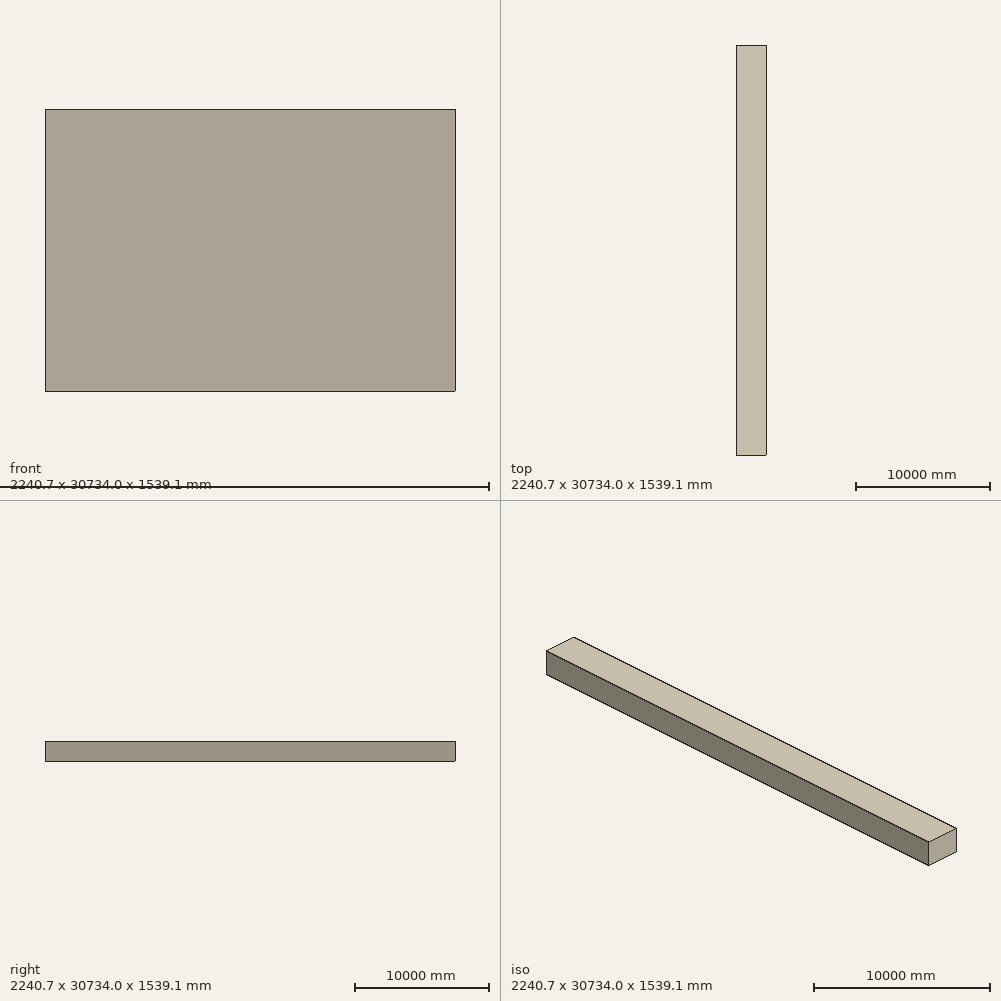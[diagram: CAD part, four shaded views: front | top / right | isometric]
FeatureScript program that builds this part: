
annotation { "Feature Type Name" : "Feature", "Feature Type Description" : "" }
export const myFeature = defineFeature(function(context is Context, id is Id, definition is map)
    precondition{}
    {
        {
            var Q0;
            Q0=qCreatedBy(makeId("Front.planeOp"),FACE);
            var sketch = newSketch(context, id + "F0", { "sketchPlane" : qUnion([Q0])});
            skLineSegment(sketch, "E0.bottom", {"start": v(-1032.38, 680.8) * mm, "end": v(1208.34, 680.8) * mm});
            skLineSegment(sketch, "E0.top", {"start": v(-1032.38, -858.27) * mm, "end": v(1208.34, -858.27) * mm});
            skLineSegment(sketch, "E0.left", {"start": v(-1032.38, 680.8) * mm, "end": v(-1032.38, -858.27) * mm});
            skLineSegment(sketch, "E0.right", {"start": v(1208.34, 680.8) * mm, "end": v(1208.34, -858.27) * mm});
            skSolve(sketch);
        }
        {
            var Q0;
            Q0=makeQuery(id+"F0.imprint","IMPRINT",FACE,{"disambiguationData":[TD([[makeQuery(id+"F0.imprint","IMPRINT",EDGE,{"derivedFrom":sQuery(id+"F0.wireOp",EDGE,"E0.bottom")}),-1.0]])]});
            extrude(context, id + "F1", {"entities" : qUnion([Q0]), "depth" : 30734 * mm});
        }
    });
